# Revit family: Haworth_Mexique_CollaborativeTable
name_source: partatom
category: Furniture
revit_build: Autodesk Revit 2018 (Build: 20170223_1515(x64)
units: mm (PartAtom-declared; Revit-internal decimal feet)

## family parameters
Always vertical = Yes
Cut with Voids When Loaded = No
OmniClass Number = 23.40.70.14.64.21
OmniClass Title = Systems Furniture
Room Calculation Point = No
Shared = No
Work Plane-Based = No

## types (2) — shared parameters
Actual Depth = 31.5 "
Actual Width = 46.5 "
Assembly Code = E2020200
Manufacturer = Haworth
Model = HCCSMXTC
Revision Number = 1
Size = Verify Final Dim. w/ Haworth
Sustainability Info = https://www.haworth.com
URL = https://www.haworth.com
URL - Product = https://www.haworth.com
Warranty = http://www.haworth.com

## per-type parameters (varying)
| type | Actual Height | Bar Height | Description | Standard Height |
| Standard Height Table | 27.6 " | No | Haworth - Cassina - Mexique - Collaborative Table - Standard Height | Yes |
| Bar Height Table | 40.2 " | Yes | Haworth - Cassina - Mexique - Collaborative Table - Bar Height | No |

## geometry (parser evidence)
native form markers: Sweep x10
no freeform markers — native parametric forms only
